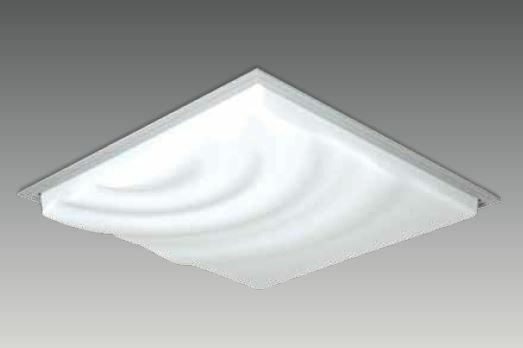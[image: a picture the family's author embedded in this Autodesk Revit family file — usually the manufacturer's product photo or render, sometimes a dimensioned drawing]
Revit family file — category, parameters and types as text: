
# Revit family: G 6060 WAV
name_source: partatom
category: Lighting Fixtures
revit_build: Autodesk Revit 2017 (Build: 20160225_1515(x64)
units: mm (PartAtom-declared; Revit-internal decimal feet)

## family parameters
Always vertical = Yes
Cut with Voids When Loaded = No
Host = Ceiling
Light Source = Yes
OmniClass Number = 23.80.70.11
OmniClass Title = Luminaries for Internal Lighting
Part Type = Normal
Room Calculation Point = No
Round Connector Dimension = Use Diameter
Shared = No

## types (4) — shared parameters
Color Filter = 16777215
Dimming Lamp Color Temperature Shift = <None>
Emit Shape Visible in Rendering = No
Emit from Rectangle Length = 540 mm  [stored 1.77165 ft]
Emit from Rectangle Width = 540 mm  [stored 1.77165 ft]
Light Source Symbol Size = 610 mm
Manufacturer = ARLIGHT
Type Image = G 6060 WAV.JPG

## per-type parameters (varying)
| type | Wattage Comments |
| GWAV.6060.36.30 | 36 |
| GWAV.6060.36.40 | 36 |
| GWAV.6060.28.30 | 28 |
| GWAV.6060.28.40 | 28 |

note: [stored X ft] marks values corroborated as IEEE doubles in the binary element streams (Revit-internal decimal feet)

## geometry (parser evidence)
native form markers: Sweep x2
no freeform markers — native parametric forms only
